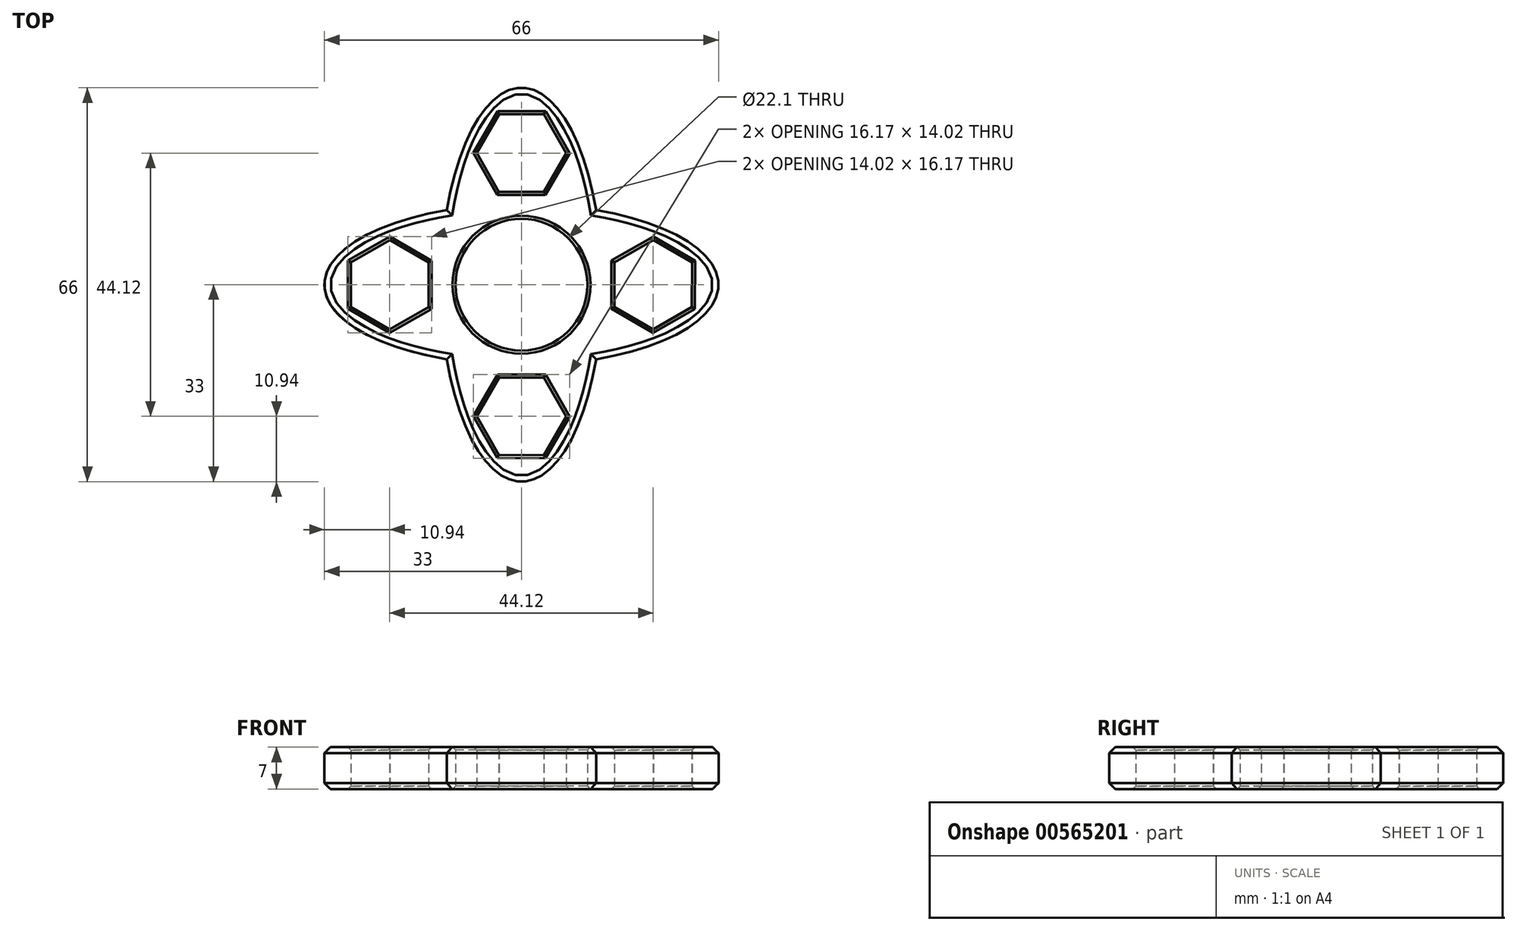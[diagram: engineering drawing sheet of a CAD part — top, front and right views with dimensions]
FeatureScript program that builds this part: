
annotation { "Feature Type Name" : "Feature", "Feature Type Description" : "" }
export const myFeature = defineFeature(function(context is Context, id is Id, definition is map)
    precondition{}
    {
        {
            var Q0;
            Q0=qCreatedBy(makeId("Top.planeOp"),FACE);
            var sketch = newSketch(context, id + "F0", { "sketchPlane" : qUnion([Q0])});
            skCircle(sketch, "E0", {"center": v(0, 0) * mm, "radius": 11.05 * mm});
            skEllipticalArc(sketch, "E1", {});
            skEllipticalArc(sketch, "E2", {});
            skLineSegment(sketch, "E3.0", {"start": v(-15.55, 3.73) * mm, "end": v(-15.57, -3.77) * mm});
            skLineSegment(sketch, "E3.1", {"start": v(-15.57, -3.77) * mm, "end": v(-22.08, -7.5) * mm});
            skLineSegment(sketch, "E3.2", {"start": v(-22.08, -7.5) * mm, "end": v(-28.57, -3.73) * mm});
            skLineSegment(sketch, "E3.3", {"start": v(-28.57, -3.73) * mm, "end": v(-28.55, 3.77) * mm});
            skLineSegment(sketch, "E3.4", {"start": v(-28.55, 3.77) * mm, "end": v(-22.04, 7.5) * mm});
            skLineSegment(sketch, "E3.5", {"start": v(-22.04, 7.5) * mm, "end": v(-15.55, 3.73) * mm});
            skPoint(sketch, "E3.0.midPoint", {"position": v(-15.56, -0.02) * mm});
            skLineSegment(sketch, "E4.1.0", {"start": v(-7.5, -22.04) * mm, "end": v(-3.73, -15.55) * mm});
            skLineSegment(sketch, "E4.1.1", {"start": v(-3.73, -15.55) * mm, "end": v(3.77, -15.57) * mm});
            skLineSegment(sketch, "E4.1.3", {"start": v(3.77, -15.57) * mm, "end": v(7.5, -22.08) * mm});
            skLineSegment(sketch, "E4.1.4", {"start": v(7.5, -22.08) * mm, "end": v(3.73, -28.57) * mm});
            skLineSegment(sketch, "E4.1.5", {"start": v(3.73, -28.57) * mm, "end": v(-3.77, -28.55) * mm});
            skLineSegment(sketch, "E4.1.6", {"start": v(-3.77, -28.55) * mm, "end": v(-7.5, -22.04) * mm});
            skLineSegment(sketch, "E4.2.0", {"start": v(22.04, -7.5) * mm, "end": v(15.55, -3.73) * mm});
            skLineSegment(sketch, "E4.2.1", {"start": v(15.55, -3.73) * mm, "end": v(15.57, 3.77) * mm});
            skLineSegment(sketch, "E4.2.3", {"start": v(15.57, 3.77) * mm, "end": v(22.08, 7.5) * mm});
            skLineSegment(sketch, "E4.2.4", {"start": v(22.08, 7.5) * mm, "end": v(28.57, 3.73) * mm});
            skLineSegment(sketch, "E4.2.5", {"start": v(28.57, 3.73) * mm, "end": v(28.55, -3.77) * mm});
            skLineSegment(sketch, "E4.2.6", {"start": v(28.55, -3.77) * mm, "end": v(22.04, -7.5) * mm});
            skLineSegment(sketch, "E4.3.0", {"start": v(7.5, 22.04) * mm, "end": v(3.73, 15.55) * mm});
            skLineSegment(sketch, "E4.3.1", {"start": v(3.73, 15.55) * mm, "end": v(-3.77, 15.57) * mm});
            skLineSegment(sketch, "E4.3.3", {"start": v(-3.77, 15.57) * mm, "end": v(-7.5, 22.08) * mm});
            skLineSegment(sketch, "E4.3.4", {"start": v(-7.5, 22.08) * mm, "end": v(-3.73, 28.57) * mm});
            skLineSegment(sketch, "E4.3.5", {"start": v(-3.73, 28.57) * mm, "end": v(3.77, 28.55) * mm});
            skLineSegment(sketch, "E4.3.6", {"start": v(3.77, 28.55) * mm, "end": v(7.5, 22.04) * mm});
            skEllipticalArc(sketch, "E5.trimOffspring", {});
            skEllipticalArc(sketch, "E6.trimOffspring", {});
            skPoint(sketch, "E7.first.point", {"position": v(-5.64, 18.83) * mm});
            skPoint(sketch, "E7.second.point", {"position": v(5.64, 18.83) * mm});
            skPoint(sketch, "E7.second.point.positionSnap0", {"position": v(-5.64, 18.83) * mm});
            skPoint(sketch, "E7.third.point", {"position": v(0, 28.56) * mm});
            skPoint(sketch, "E8.first.point", {"position": v(-28.56, 0) * mm});
            skPoint(sketch, "E8.second.point", {"position": v(-18.8, 5.62) * mm});
            skPoint(sketch, "E8.third.point", {"position": v(-18.8, -5.62) * mm});
            skPoint(sketch, "E8.third.point.positionSnap0", {"position": v(-18.8, 5.62) * mm});
            skPoint(sketch, "E9.first.point", {"position": v(-5.64, -25.3) * mm});
            skPoint(sketch, "E9.second.point", {"position": v(0, -15.56) * mm});
            skPoint(sketch, "E9.third.point", {"position": v(5.64, -25.3) * mm});
            skPoint(sketch, "E9.third.point.positionSnap0", {"position": v(-5.64, -25.3) * mm});
            skPoint(sketch, "E10.first.point", {"position": v(18.8, -5.62) * mm});
            skPoint(sketch, "E10.second.point", {"position": v(18.8, 5.64) * mm});
            skPoint(sketch, "E10.second.point.positionSnap0", {"position": v(18.83, 5.64) * mm});
            skPoint(sketch, "E10.second.point.positionSnap1", {"position": v(18.8, -5.62) * mm});
            skPoint(sketch, "E10.third.point", {"position": v(25.3, 5.64) * mm});
            skPoint(sketch, "E10.third.point.positionSnap0", {"position": v(18.83, 5.64) * mm});
            const initialGuessF0  = {"E1": [0, 0, 0, -1, 0.033, 0.0135, 5.100707698557156, 1.1824776086224302], "E2": [0, 0, 1, 0, 0.033, 0.0135, 1.9591150449673624, 4.324070262212223], "E5.trimOffspring": [0, 0, 0, -1, 0.033, 0.0135, 1.959115044967362, 4.324070262212223], "E6.trimOffspring": [0, 0, 1, 0, 0.033, 0.0135, 5.100707698557155, 1.1824776086224305]};
            skSetInitialGuess(sketch, initialGuessF0);
            skSolve(sketch);
        }
        {
            var Q0;
            Q0=makeQuery(id+"F0.imprint","IMPRINT",FACE,{"disambiguationData":[TD([[makeQuery(id+"F0.imprint","IMPRINT",EDGE,{"derivedFrom":sQuery(id+"F0.wireOp",EDGE,"E0")}),-1.0]])]});
            extrude(context, id + "F1", {"entities" : qUnion([Q0]), "depth" : 7 * mm, "offsetDistance" : 25 * mm});
        }
        {
            var Q0;
            Q0=makeQuery(id+"F1.opExtrude","CAP_EDGE",EDGE,{"disambiguationData":[OSD([sQuery(id+"F0.wireOp",EDGE,"E2")])],"isStart":false});
            var Q1;
            Q1=makeQuery(id+"F1.opExtrude","CAP_EDGE",EDGE,{"disambiguationData":[OSD([sQuery(id+"F0.wireOp",EDGE,"E1")])],"isStart":false});
            var Q2;
            Q2=makeQuery(id+"F1.opExtrude","CAP_EDGE",EDGE,{"disambiguationData":[OSD([sQuery(id+"F0.wireOp",EDGE,"E6.trimOffspring")])],"isStart":false});
            var Q3;
            Q3=makeQuery(id+"F1.opExtrude","CAP_EDGE",EDGE,{"disambiguationData":[OSD([sQuery(id+"F0.wireOp",EDGE,"E5.trimOffspring")])],"isStart":false});
            var Q4;
            Q4=makeQuery(id+"F1.opExtrude","CAP_EDGE",EDGE,{"disambiguationData":[OSD([sQuery(id+"F0.wireOp",EDGE,"E5.trimOffspring")])],"isStart":true});
            var Q5;
            Q5=makeQuery(id+"F1.opExtrude","CAP_EDGE",EDGE,{"disambiguationData":[OSD([sQuery(id+"F0.wireOp",EDGE,"E6.trimOffspring")])],"isStart":true});
            var Q6;
            Q6=makeQuery(id+"F1.opExtrude","CAP_EDGE",EDGE,{"disambiguationData":[OSD([sQuery(id+"F0.wireOp",EDGE,"E1")])],"isStart":true});
            var Q7;
            Q7=makeQuery(id+"F1.opExtrude","CAP_EDGE",EDGE,{"disambiguationData":[OSD([sQuery(id+"F0.wireOp",EDGE,"E2")])],"isStart":true});
            chamfer(context, id + "F2", {"entities" : qUnion([Q0, Q1, Q2, Q3, Q4, Q5, Q6, Q7]), "width" : 1 * mm, "tangentPropagation" : true});
        }
        {
            var Q0;
            Q0=makeQuery(id+"F1.opExtrude","SWEPT_FACE",FACE,{"disambiguationData":[OSD([sQuery(id+"F0.wireOp",EDGE,"E0")])]});
            chamfer(context, id + "F3", {"entities" : qUnion([Q0]), "width" : 0.5 * mm, "tangentPropagation" : true});
        }
        {
            var Q0;
            Q0=makeQuery(id+"F1.opExtrude","CAP_EDGE",EDGE,{"disambiguationData":[OSD([sQuery(id+"F0.wireOp",EDGE,"E4.1.0")])],"isStart":true});
            var Q1;
            Q1=makeQuery(id+"F1.opExtrude","CAP_EDGE",EDGE,{"disambiguationData":[OSD([sQuery(id+"F0.wireOp",EDGE,"E4.1.6")])],"isStart":true});
            var Q2;
            Q2=makeQuery(id+"F1.opExtrude","CAP_EDGE",EDGE,{"disambiguationData":[OSD([sQuery(id+"F0.wireOp",EDGE,"E4.1.5")])],"isStart":true});
            var Q3;
            Q3=makeQuery(id+"F1.opExtrude","CAP_EDGE",EDGE,{"disambiguationData":[OSD([sQuery(id+"F0.wireOp",EDGE,"E4.1.4")])],"isStart":true});
            var Q4;
            Q4=makeQuery(id+"F1.opExtrude","CAP_EDGE",EDGE,{"disambiguationData":[OSD([sQuery(id+"F0.wireOp",EDGE,"E4.1.3")])],"isStart":true});
            var Q5;
            Q5=makeQuery(id+"F1.opExtrude","CAP_EDGE",EDGE,{"disambiguationData":[OSD([sQuery(id+"F0.wireOp",EDGE,"E4.1.1")])],"isStart":true});
            var Q6;
            Q6=makeQuery(id+"F1.opExtrude","CAP_EDGE",EDGE,{"disambiguationData":[OSD([sQuery(id+"F0.wireOp",EDGE,"E4.2.0")])],"isStart":true});
            var Q7;
            Q7=makeQuery(id+"F1.opExtrude","CAP_EDGE",EDGE,{"disambiguationData":[OSD([sQuery(id+"F0.wireOp",EDGE,"E4.2.6")])],"isStart":true});
            var Q8;
            Q8=makeQuery(id+"F1.opExtrude","CAP_EDGE",EDGE,{"disambiguationData":[OSD([sQuery(id+"F0.wireOp",EDGE,"E4.2.5")])],"isStart":true});
            var Q9;
            Q9=makeQuery(id+"F1.opExtrude","CAP_EDGE",EDGE,{"disambiguationData":[OSD([sQuery(id+"F0.wireOp",EDGE,"E4.2.4")])],"isStart":true});
            var Q10;
            Q10=makeQuery(id+"F1.opExtrude","CAP_EDGE",EDGE,{"disambiguationData":[OSD([sQuery(id+"F0.wireOp",EDGE,"E4.2.3")])],"isStart":true});
            var Q11;
            Q11=makeQuery(id+"F1.opExtrude","CAP_EDGE",EDGE,{"disambiguationData":[OSD([sQuery(id+"F0.wireOp",EDGE,"E4.2.1")])],"isStart":true});
            var Q12;
            Q12=makeQuery(id+"F1.opExtrude","CAP_EDGE",EDGE,{"disambiguationData":[OSD([sQuery(id+"F0.wireOp",EDGE,"E4.2.0")])],"isStart":false});
            var Q13;
            Q13=makeQuery(id+"F1.opExtrude","CAP_EDGE",EDGE,{"disambiguationData":[OSD([sQuery(id+"F0.wireOp",EDGE,"E4.2.6")])],"isStart":false});
            var Q14;
            Q14=makeQuery(id+"F1.opExtrude","CAP_EDGE",EDGE,{"disambiguationData":[OSD([sQuery(id+"F0.wireOp",EDGE,"E4.2.5")])],"isStart":false});
            var Q15;
            Q15=makeQuery(id+"F1.opExtrude","CAP_EDGE",EDGE,{"disambiguationData":[OSD([sQuery(id+"F0.wireOp",EDGE,"E4.2.1")])],"isStart":false});
            var Q16;
            Q16=makeQuery(id+"F1.opExtrude","CAP_EDGE",EDGE,{"disambiguationData":[OSD([sQuery(id+"F0.wireOp",EDGE,"E4.2.3")])],"isStart":false});
            var Q17;
            Q17=makeQuery(id+"F1.opExtrude","CAP_EDGE",EDGE,{"disambiguationData":[OSD([sQuery(id+"F0.wireOp",EDGE,"E4.2.4")])],"isStart":false});
            var Q18;
            Q18=makeQuery(id+"F1.opExtrude","CAP_EDGE",EDGE,{"disambiguationData":[OSD([sQuery(id+"F0.wireOp",EDGE,"E4.1.1")])],"isStart":false});
            var Q19;
            Q19=makeQuery(id+"F1.opExtrude","CAP_EDGE",EDGE,{"disambiguationData":[OSD([sQuery(id+"F0.wireOp",EDGE,"E4.1.3")])],"isStart":false});
            var Q20;
            Q20=makeQuery(id+"F1.opExtrude","CAP_EDGE",EDGE,{"disambiguationData":[OSD([sQuery(id+"F0.wireOp",EDGE,"E4.1.4")])],"isStart":false});
            var Q21;
            Q21=makeQuery(id+"F1.opExtrude","CAP_EDGE",EDGE,{"disambiguationData":[OSD([sQuery(id+"F0.wireOp",EDGE,"E4.1.5")])],"isStart":false});
            var Q22;
            Q22=makeQuery(id+"F1.opExtrude","CAP_EDGE",EDGE,{"disambiguationData":[OSD([sQuery(id+"F0.wireOp",EDGE,"E4.1.6")])],"isStart":false});
            var Q23;
            Q23=makeQuery(id+"F1.opExtrude","CAP_EDGE",EDGE,{"disambiguationData":[OSD([sQuery(id+"F0.wireOp",EDGE,"E4.1.0")])],"isStart":false});
            var Q24;
            Q24=makeQuery(id+"F1.opExtrude","CAP_EDGE",EDGE,{"disambiguationData":[OSD([sQuery(id+"F0.wireOp",EDGE,"E3.2")])],"isStart":false});
            var Q25;
            Q25=makeQuery(id+"F1.opExtrude","CAP_EDGE",EDGE,{"disambiguationData":[OSD([sQuery(id+"F0.wireOp",EDGE,"E3.2")])],"isStart":true});
            var Q26;
            Q26=makeQuery(id+"F1.opExtrude","CAP_EDGE",EDGE,{"disambiguationData":[OSD([sQuery(id+"F0.wireOp",EDGE,"E3.3")])],"isStart":true});
            var Q27;
            Q27=makeQuery(id+"F1.opExtrude","CAP_EDGE",EDGE,{"disambiguationData":[OSD([sQuery(id+"F0.wireOp",EDGE,"E3.3")])],"isStart":false});
            var Q28;
            Q28=makeQuery(id+"F1.opExtrude","CAP_EDGE",EDGE,{"disambiguationData":[OSD([sQuery(id+"F0.wireOp",EDGE,"E3.4")])],"isStart":true});
            var Q29;
            Q29=makeQuery(id+"F1.opExtrude","CAP_EDGE",EDGE,{"disambiguationData":[OSD([sQuery(id+"F0.wireOp",EDGE,"E3.4")])],"isStart":false});
            var Q30;
            Q30=makeQuery(id+"F1.opExtrude","CAP_EDGE",EDGE,{"disambiguationData":[OSD([sQuery(id+"F0.wireOp",EDGE,"E3.5")])],"isStart":false});
            var Q31;
            Q31=makeQuery(id+"F1.opExtrude","CAP_EDGE",EDGE,{"disambiguationData":[OSD([sQuery(id+"F0.wireOp",EDGE,"E3.5")])],"isStart":true});
            var Q32;
            Q32=makeQuery(id+"F1.opExtrude","CAP_EDGE",EDGE,{"disambiguationData":[OSD([sQuery(id+"F0.wireOp",EDGE,"E3.0")])],"isStart":true});
            var Q33;
            Q33=makeQuery(id+"F1.opExtrude","CAP_EDGE",EDGE,{"disambiguationData":[OSD([sQuery(id+"F0.wireOp",EDGE,"E3.0")])],"isStart":false});
            var Q34;
            Q34=makeQuery(id+"F1.opExtrude","CAP_EDGE",EDGE,{"disambiguationData":[OSD([sQuery(id+"F0.wireOp",EDGE,"E3.1")])],"isStart":false});
            var Q35;
            Q35=makeQuery(id+"F1.opExtrude","CAP_EDGE",EDGE,{"disambiguationData":[OSD([sQuery(id+"F0.wireOp",EDGE,"E3.1")])],"isStart":true});
            var Q36;
            Q36=makeQuery(id+"F1.opExtrude","CAP_EDGE",EDGE,{"disambiguationData":[OSD([sQuery(id+"F0.wireOp",EDGE,"E4.3.0")])],"isStart":true});
            var Q37;
            Q37=makeQuery(id+"F1.opExtrude","CAP_EDGE",EDGE,{"disambiguationData":[OSD([sQuery(id+"F0.wireOp",EDGE,"E4.3.1")])],"isStart":true});
            var Q38;
            Q38=makeQuery(id+"F1.opExtrude","CAP_EDGE",EDGE,{"disambiguationData":[OSD([sQuery(id+"F0.wireOp",EDGE,"E4.3.3")])],"isStart":true});
            var Q39;
            Q39=makeQuery(id+"F1.opExtrude","CAP_EDGE",EDGE,{"disambiguationData":[OSD([sQuery(id+"F0.wireOp",EDGE,"E4.3.4")])],"isStart":true});
            var Q40;
            Q40=makeQuery(id+"F1.opExtrude","CAP_EDGE",EDGE,{"disambiguationData":[OSD([sQuery(id+"F0.wireOp",EDGE,"E4.3.5")])],"isStart":true});
            var Q41;
            Q41=makeQuery(id+"F1.opExtrude","CAP_EDGE",EDGE,{"disambiguationData":[OSD([sQuery(id+"F0.wireOp",EDGE,"E4.3.6")])],"isStart":true});
            var Q42;
            Q42=makeQuery(id+"F1.opExtrude","CAP_EDGE",EDGE,{"disambiguationData":[OSD([sQuery(id+"F0.wireOp",EDGE,"E4.3.0")])],"isStart":false});
            var Q43;
            Q43=makeQuery(id+"F1.opExtrude","CAP_EDGE",EDGE,{"disambiguationData":[OSD([sQuery(id+"F0.wireOp",EDGE,"E4.3.6")])],"isStart":false});
            var Q44;
            Q44=makeQuery(id+"F1.opExtrude","CAP_EDGE",EDGE,{"disambiguationData":[OSD([sQuery(id+"F0.wireOp",EDGE,"E4.3.4")])],"isStart":false});
            var Q45;
            Q45=makeQuery(id+"F1.opExtrude","CAP_EDGE",EDGE,{"disambiguationData":[OSD([sQuery(id+"F0.wireOp",EDGE,"E4.3.3")])],"isStart":false});
            var Q46;
            Q46=makeQuery(id+"F1.opExtrude","CAP_EDGE",EDGE,{"disambiguationData":[OSD([sQuery(id+"F0.wireOp",EDGE,"E4.3.5")])],"isStart":false});
            var Q47;
            Q47=makeQuery(id+"F1.opExtrude","CAP_EDGE",EDGE,{"disambiguationData":[OSD([sQuery(id+"F0.wireOp",EDGE,"E4.3.1")])],"isStart":false});
            chamfer(context, id + "F4", {"entities" : qUnion([Q0, Q1, Q2, Q3, Q4, Q5, Q6, Q7, Q8, Q9, Q10, Q11, Q12, Q13, Q14, Q15, Q16, Q17, Q18, Q19, Q20, Q21, Q22, Q23, Q24, Q25, Q26, Q27, Q28, Q29, Q30, Q31, Q32, Q33, Q34, Q35, Q36, Q37, Q38, Q39, Q40, Q41, Q42, Q43, Q44, Q45, Q46, Q47]), "width" : 0.5 * mm, "tangentPropagation" : true});
        }
    });
